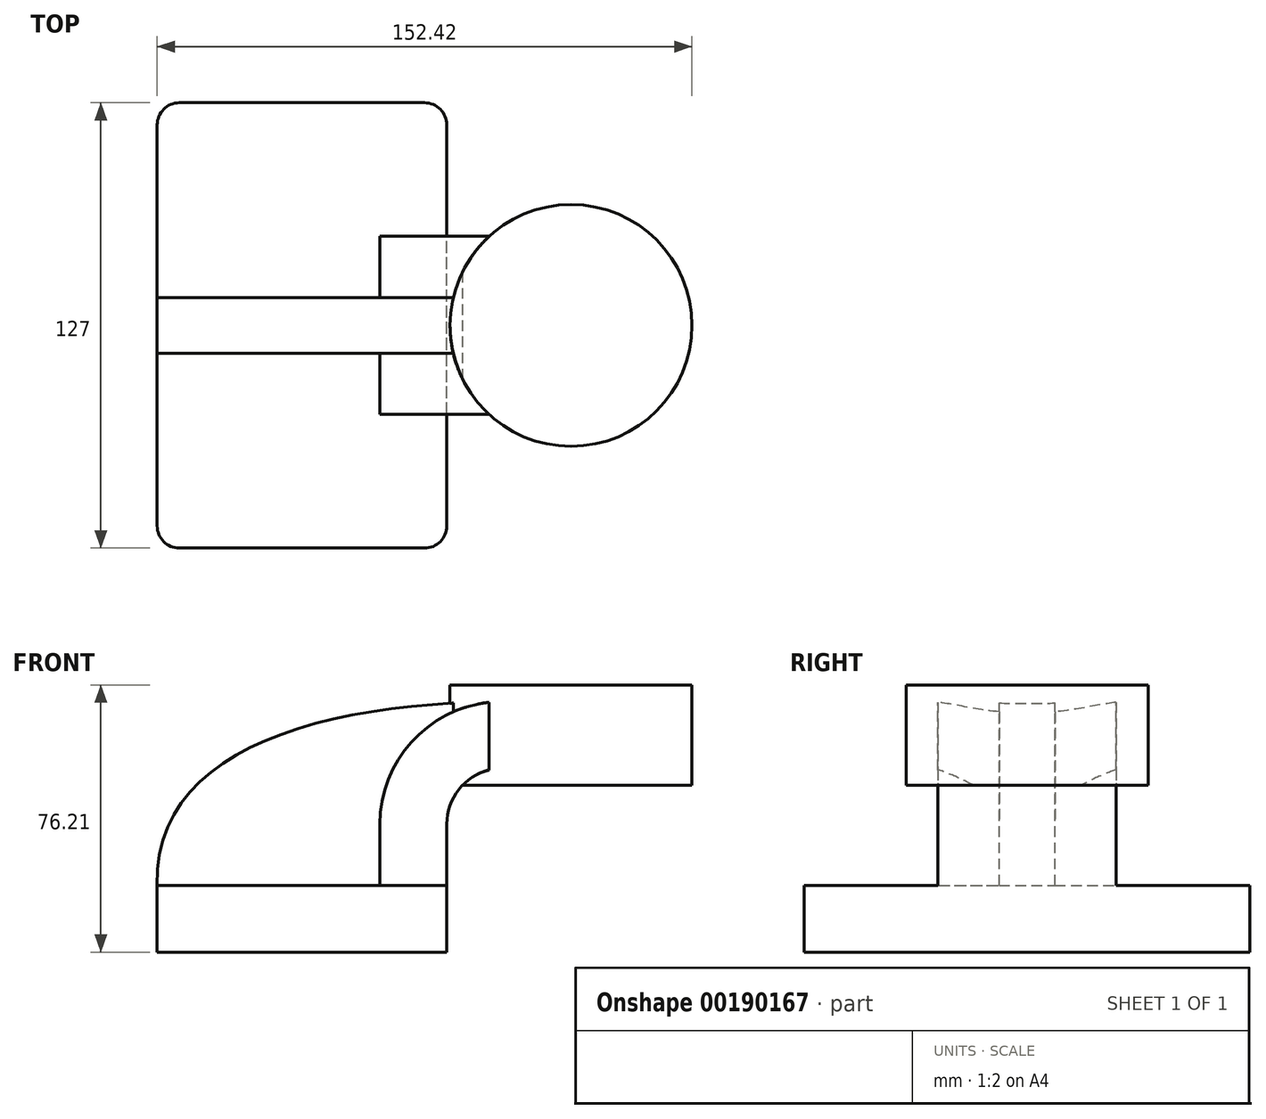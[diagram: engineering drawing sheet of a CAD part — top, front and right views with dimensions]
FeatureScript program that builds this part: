
annotation { "Feature Type Name" : "Feature", "Feature Type Description" : "" }
export const myFeature = defineFeature(function(context is Context, id is Id, definition is map)
    precondition{}
    {
        {
            var Q0;
            Q0=qCreatedBy(makeId("Front.planeOp"),FACE);
            var sketch = newSketch(context, id + "F0", { "sketchPlane" : qUnion([Q0])});
            skLineSegment(sketch, "E0.bottom", {"start": v(-41.28, 9.52) * mm, "end": v(41.28, 9.53) * mm});
            skLineSegment(sketch, "E0.top", {"start": v(-41.28, -9.53) * mm, "end": v(41.28, -9.53) * mm});
            skLineSegment(sketch, "E0.left", {"start": v(-41.28, 9.52) * mm, "end": v(-41.28, -9.53) * mm});
            skLineSegment(sketch, "E0.right", {"start": v(41.28, 9.53) * mm, "end": v(41.28, -9.52) * mm});
            skPoint(sketch, "E0.middle", {"position": v(0, 0) * mm});
            skLineSegment(sketch, "E1.bottom", {"start": v(60.32, 38.1) * mm, "end": v(111.12, 38.1) * mm});
            skLineSegment(sketch, "E1.top", {"start": v(60.32, 66.68) * mm, "end": v(111.12, 66.68) * mm});
            skLineSegment(sketch, "E1.left", {"start": v(60.32, 38.1) * mm, "end": v(60.32, 66.68) * mm});
            skLineSegment(sketch, "E1.right", {"start": v(111.12, 38.1) * mm, "end": v(111.12, 66.68) * mm});
            skPoint(sketch, "E1.middle", {"position": v(85.72, 52.39) * mm});
            skLineSegment(sketch, "E2", {"start": v(41.27, 9.53) * mm, "end": v(41.27, 27) * mm});
            skArc(sketch, "E3", {"start": v(41.27, 27) * mm, "mid": v(45.92, 38.23) * mm, "end": v(57.15, 42.88) * mm});
            skLineSegment(sketch, "E4", {"start": v(57.15, 42.88) * mm, "end": v(76.65, 42.88) * mm});
            skLineSegment(sketch, "E5.0", {"start": v(57.15, 61.93) * mm, "end": v(76.65, 61.93) * mm});
            skArc(sketch, "E5.1", {"start": v(22.23, 27) * mm, "mid": v(32.45, 51.7) * mm, "end": v(57.15, 61.93) * mm});
            skLineSegment(sketch, "E5.2", {"start": v(22.23, 9.53) * mm, "end": v(22.23, 27) * mm});
            skLineSegment(sketch, "E6", {"start": v(76.65, 61.93) * mm, "end": v(76.65, 42.88) * mm});
            skFitSpline(sketch, "E7", {"points": [v(-41.28, 9.52) * mm, v(57.15, 61.93) * mm], "startDerivative": vector(-3.1, 116.3) * mm, "endDerivative": vector(156.06, 1.15) * mm});
            skLineSegment(sketch, "E8", {"start": v(76.65, 66.68) * mm, "end": v(76.65, 38.1) * mm});
            skSolve(sketch);
        }
        {
            var Q0;
            Q0=makeQuery(id+"F0.imprint","IMPRINT",FACE,{"disambiguationData":[TD([[makeQuery(id+"F0.imprint","IMPRINT",EDGE,{"derivedFrom":sQuery(id+"F0.wireOp",EDGE,"E0.top")}),1.0]])]});
            extrude(context, id + "F1", {"entities" : qUnion([Q0]), "endBound" : BoundingType.SYMMETRIC, "depth" : 127 * mm});
        }
        {
            var Q0;
            {var subQ1=sQuery(id+"F0.wireOp",EDGE,"E2");Q0=makeQuery(id+"F0.imprint","IMPRINT",FACE,{"disambiguationData":[TD([[makeQuery(id+"F0.imprint","IMPRINT",EDGE,{"derivedFrom":subQ1}),1.0]])]});}
            var Q1;
            {var subQ5=sQuery(id+"F0.wireOp",EDGE,"E6");Q1=makeQuery(id+"F0.imprint","IMPRINT",FACE,{"disambiguationData":[TD([[makeQuery(id+"F0.imprint","IMPRINT",EDGE,{"derivedFrom":subQ5}),-1.0]])]});}
            extrude(context, id + "F2", {"entities" : qUnion([Q0, Q1]), "operationType" : NewBodyOperationType.ADD, "endBound" : BoundingType.SYMMETRIC, "depth" : 50.8 * mm});
        }
        {
            var Q0;
            {var subQ3=sQuery(id+"F0.wireOp",EDGE,"E5.2");Q0=makeQuery(id+"F0.imprint","IMPRINT",FACE,{"disambiguationData":[TD([[makeQuery(id+"F0.imprint","IMPRINT",EDGE,{"derivedFrom":subQ3}),1.0]])]});}
            extrude(context, id + "F3", {"entities" : qUnion([Q0]), "operationType" : NewBodyOperationType.ADD, "endBound" : BoundingType.SYMMETRIC, "depth" : 15.88 * mm});
        }
        {
            var Q0;
            {var subQ0=sQuery(id+"F0.wireOp",EDGE,"E1.right");Q0=makeQuery(id+"F0.imprint","IMPRINT",FACE,{"disambiguationData":[TD([[makeQuery(id+"F0.imprint","IMPRINT",EDGE,{"derivedFrom":subQ0}),1.0]])]});}
            var Q1;
            Q1=sQuery(id+"F0.wireOp",EDGE,"E8");
            revolve(context, id + "F4", {"operationType" : NewBodyOperationType.ADD, "entities" : qUnion([Q0]), "axis" : qUnion([Q1]), "revolveType" : RevolveType.FULL});
        }
        {
            var Q0;
            Q0=makeQuery(id+"F1.opExtrude","CAP_EDGE",EDGE,{"disambiguationData":[OSD([sQuery(id+"F0.wireOp",EDGE,"E0.right")])],"isStart":true});
            var Q1;
            Q1=makeQuery(id+"F1.opExtrude","CAP_EDGE",EDGE,{"disambiguationData":[OSD([sQuery(id+"F0.wireOp",EDGE,"E0.right")])],"isStart":false});
            var Q2;
            Q2=makeQuery(id+"F1.opExtrude","CAP_EDGE",EDGE,{"disambiguationData":[OSD([sQuery(id+"F0.wireOp",EDGE,"E0.left")])],"isStart":true});
            var Q3;
            Q3=makeQuery(id+"F1.opExtrude","CAP_EDGE",EDGE,{"disambiguationData":[OSD([sQuery(id+"F0.wireOp",EDGE,"E0.left")])],"isStart":false});
            fillet(context, id + "F5", {"entities" : qUnion([Q0, Q1, Q2, Q3]), "radius" : 6.35 * mm, "tangentPropagation" : true, "allowEdgeOverflow" : false});
        }
    });
